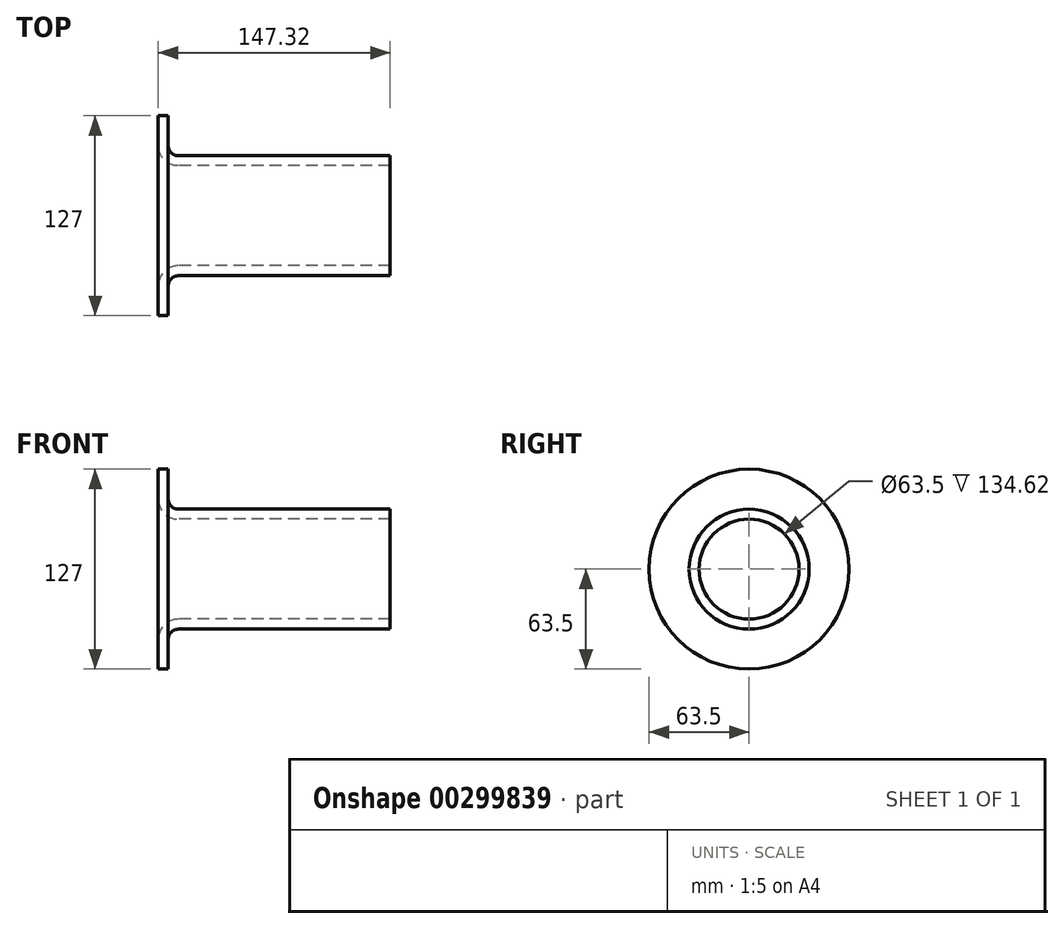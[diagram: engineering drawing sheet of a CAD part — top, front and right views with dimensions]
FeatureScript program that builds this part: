
annotation { "Feature Type Name" : "Feature", "Feature Type Description" : "" }
export const myFeature = defineFeature(function(context is Context, id is Id, definition is map)
    precondition{}
    {
        {
            var Q0;
            Q0=qCreatedBy(makeId("Front.planeOp"),FACE);
            var sketch = newSketch(context, id + "F0", { "sketchPlane" : qUnion([Q0])});
            skPoint(sketch, "E0", {"position": v(147.32, 38.1) * mm});
            skLineSegment(sketch, "E1", {"start": v(147.32, 38.1) * mm, "end": v(12.7, 38.1) * mm});
            skLineSegment(sketch, "E2", {"start": v(6.35, 63.5) * mm, "end": v(6.35, 44.45) * mm});
            skPoint(sketch, "E3", {"position": v(12.7, 44.45) * mm});
            skArc(sketch, "E4", {"start": v(6.35, 44.45) * mm, "mid": v(8.2, 39.96) * mm, "end": v(12.7, 38.1) * mm});
            skLineSegment(sketch, "E5.0", {"start": v(147.32, 31.75) * mm, "end": v(12.7, 31.75) * mm});
            skArc(sketch, "E5.1", {"start": v(0, 44.45) * mm, "mid": v(3.72, 35.47) * mm, "end": v(12.7, 31.75) * mm});
            skLineSegment(sketch, "E5.2", {"start": v(0, 63.5) * mm, "end": v(0, 44.45) * mm});
            skLineSegment(sketch, "E6", {"start": v(0, 63.5) * mm, "end": v(6.35, 63.5) * mm});
            skLineSegment(sketch, "E7", {"start": v(147.32, 38.1) * mm, "end": v(147.32, 31.75) * mm});
            skLineSegment(sketch, "E8", {"start": v(0, 0) * mm, "end": v(26.85, 0) * mm});
            skSolve(sketch);
        }
        {
            var Q0;
            Q0 = qSketchRegion(id + "F0", true);
            var Q1;
            Q1=sQuery(id+"F0.wireOp",EDGE,"E8");
            revolve(context, id + "F1", {"entities" : qUnion([Q0]), "axis" : qUnion([Q1]), "revolveType" : RevolveType.FULL});
        }
    });
